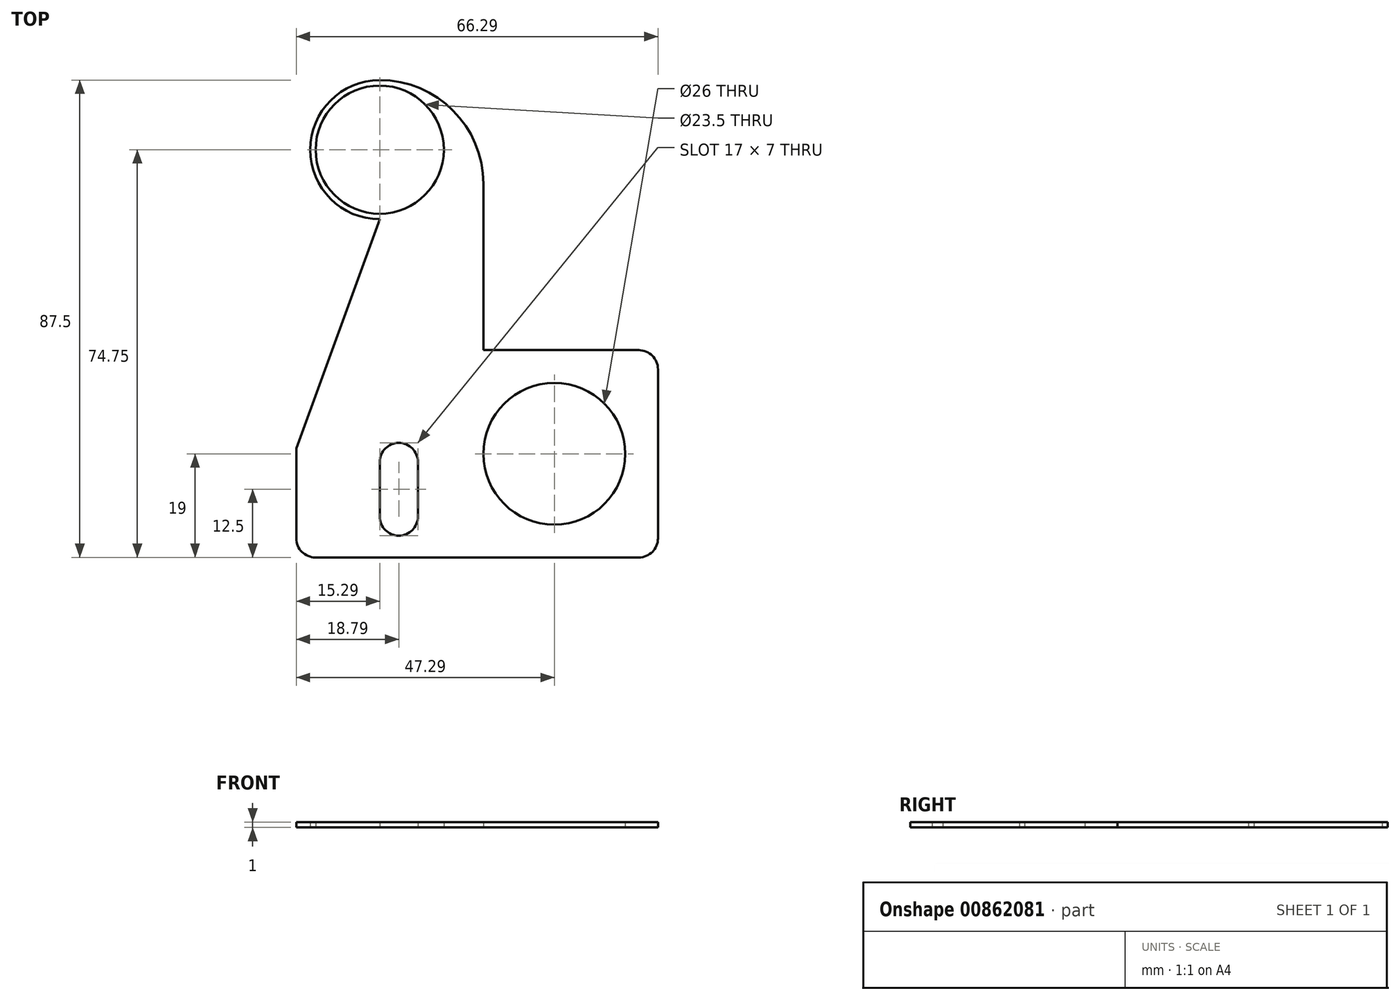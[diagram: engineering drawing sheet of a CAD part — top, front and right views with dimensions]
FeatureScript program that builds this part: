
annotation { "Feature Type Name" : "Feature", "Feature Type Description" : "" }
export const myFeature = defineFeature(function(context is Context, id is Id, definition is map)
    precondition{}
    {
        {
            var Q0;
            Q0=qCreatedBy(makeId("Top.planeOp"),FACE);
            var sketch = newSketch(context, id + "F0", { "sketchPlane" : qUnion([Q0])});
            skLineSegment(sketch, "E0.bottom", {"start": v(-3.5, 0) * mm, "end": v(-3.5, 0) * mm});
            skLineSegment(sketch, "E0.top", {"start": v(-3.5, -17) * mm, "end": v(-3.5, -17) * mm});
            skLineSegment(sketch, "E0.left", {"start": v(0, -3.5) * mm, "end": v(0, -13.5) * mm});
            skLineSegment(sketch, "E0.right", {"start": v(-7, -3.5) * mm, "end": v(-7, -13.5) * mm});
            skLineSegment(sketch, "E1", {"start": v(-7, -8.5) * mm, "end": v(12, -8.5) * mm, "construction": true});
            skLineSegment(sketch, "E2", {"start": v(12, -8.5) * mm, "end": v(12, 47.5) * mm, "construction": true});
            skCircle(sketch, "E3", {"center": v(25, -2) * mm, "radius": 13 * mm});
            skPoint(sketch, "E3.first.point", {"position": v(12, -2) * mm});
            skPoint(sketch, "E3.second.point", {"position": v(37.9, -3.6) * mm});
            skPoint(sketch, "E3.third.point", {"position": v(37.68, 0.87) * mm});
            skLineSegment(sketch, "E4", {"start": v(25, -2) * mm, "end": v(44, -2) * mm, "construction": true});
            skLineSegment(sketch, "E5", {"start": v(25, -2) * mm, "end": v(25, 17) * mm, "construction": true});
            skLineSegment(sketch, "E6", {"start": v(25, -2) * mm, "end": v(25, -21) * mm, "construction": true});
            skLineSegment(sketch, "E7", {"start": v(-7, 0) * mm, "end": v(-7, 68) * mm, "construction": true});
            skLineSegment(sketch, "E8", {"start": v(0, 0) * mm, "end": v(0, 42) * mm, "construction": true});
            skLineSegment(sketch, "E9", {"start": v(0, 42) * mm, "end": v(-44.98, 42) * mm, "construction": true});
            skLineSegment(sketch, "E10", {"start": v(-26.45, 42) * mm, "end": v(-26.45, 65.5) * mm, "construction": true});
            skLineSegment(sketch, "E11", {"start": v(-26.45, 65.5) * mm, "end": v(23.74, 65.5) * mm, "construction": true});
            skLineSegment(sketch, "E12", {"start": v(-26.45, 53.75) * mm, "end": v(22.45, 53.75) * mm, "construction": true});
            skCircle(sketch, "E13", {"center": v(-7, 53.75) * mm, "radius": 11.75 * mm});
            skCircle(sketch, "E14", {"center": v(-7, 53.75) * mm, "radius": 12.75 * mm});
            skLineSegment(sketch, "E15", {"start": v(68.55, 0) * mm, "end": v(68.55, 44) * mm, "construction": true});
            skLineSegment(sketch, "E16", {"start": v(68.55, 44) * mm, "end": v(4.14, 44) * mm, "construction": true});
            skLineSegment(sketch, "E17", {"start": v(-7, 41) * mm, "end": v(-22.29, -1) * mm});
            skLineSegment(sketch, "E18", {"start": v(-14.22, 42) * mm, "end": v(-14.22, -1) * mm, "construction": true});
            skLineSegment(sketch, "E19", {"start": v(-14.22, -1) * mm, "end": v(-39.76, -1) * mm, "construction": true});
            skLineSegment(sketch, "E20", {"start": v(-7, -17) * mm, "end": v(-7, -21) * mm, "construction": true});
            skLineSegment(sketch, "E21", {"start": v(-7, -21) * mm, "end": v(-18.79, -21) * mm, "construction": true});
            skLineSegment(sketch, "E22", {"start": v(44, -2) * mm, "end": v(44, -17.5) * mm, "construction": true});
            skLineSegment(sketch, "E23", {"start": v(25, 17) * mm, "end": v(40.5, 17) * mm, "construction": true});
            skPoint(sketch, "E24", {"position": v(-7, 66.5) * mm});
            skArc(sketch, "E25", {"start": v(12, 47.5) * mm, "mid": v(6.44, 60.94) * mm, "end": v(-7, 66.5) * mm});
            skLineSegment(sketch, "E26", {"start": v(-22.29, -1) * mm, "end": v(-22.29, -17.5) * mm});
            skLineSegment(sketch, "E27", {"start": v(-18.79, -21) * mm, "end": v(40.5, -21) * mm});
            skLineSegment(sketch, "E28", {"start": v(44, -17.5) * mm, "end": v(44, 13.5) * mm});
            skLineSegment(sketch, "E29", {"start": v(40.5, 17) * mm, "end": v(12, 17) * mm});
            skLineSegment(sketch, "E30", {"start": v(12, 17) * mm, "end": v(12, 47.5) * mm});
            skPoint(sketch, "E31.visualSharp", {"position": v(-7, 0) * mm});
            skArc(sketch, "E31.filletArc", {"start": v(-3.5, 0) * mm, "mid": v(-5.97, -1.03) * mm, "end": v(-7, -3.5) * mm});
            skPoint(sketch, "E32.visualSharp", {"position": v(0, 0) * mm});
            skArc(sketch, "E32.filletArc", {"start": v(0, -3.5) * mm, "mid": v(-1.03, -1.03) * mm, "end": v(-3.5, 0) * mm});
            skPoint(sketch, "E33.visualSharp", {"position": v(0, -17) * mm});
            skArc(sketch, "E33.filletArc", {"start": v(-3.5, -17) * mm, "mid": v(-1.03, -15.97) * mm, "end": v(0, -13.5) * mm});
            skPoint(sketch, "E34.visualSharp", {"position": v(-7, -17) * mm});
            skArc(sketch, "E34.filletArc", {"start": v(-7, -13.5) * mm, "mid": v(-5.97, -15.97) * mm, "end": v(-3.5, -17) * mm});
            skArc(sketch, "E35.filletArc", {"start": v(-22.29, -17.5) * mm, "mid": v(-21.26, -19.97) * mm, "end": v(-18.79, -21) * mm});
            skArc(sketch, "E36.filletArc", {"start": v(40.5, -21) * mm, "mid": v(42.97, -19.97) * mm, "end": v(44, -17.5) * mm});
            skArc(sketch, "E37.filletArc", {"start": v(44, 13.5) * mm, "mid": v(42.97, 15.97) * mm, "end": v(40.5, 17) * mm});
            skLineSegment(sketch, "E38", {"start": v(25, -2) * mm, "end": v(6.1, -2) * mm, "construction": true});
            skSolve(sketch);
        }
        {
            var Q0;
            Q0=makeQuery(id+"F0.imprint","IMPRINT",FACE,{"disambiguationData":[TD([[makeQuery(id+"F0.imprint","IMPRINT",EDGE,{"derivedFrom":sQuery(id+"F0.wireOp",EDGE,"E0.left")}),1.0]])]});
            var Q1;
            Q1=makeQuery(id+"F0.imprint","IMPRINT",FACE,{"disambiguationData":[TD([[makeQuery(id+"F0.imprint","IMPRINT",EDGE,{"derivedFrom":sQuery(id+"F0.wireOp",EDGE,"E13")}),-1.0]])]});
            extrude(context, id + "F1", {"entities" : qUnion([Q0, Q1]), "depth" : 1 * mm, "offsetDistance" : 25 * mm});
        }
    });
